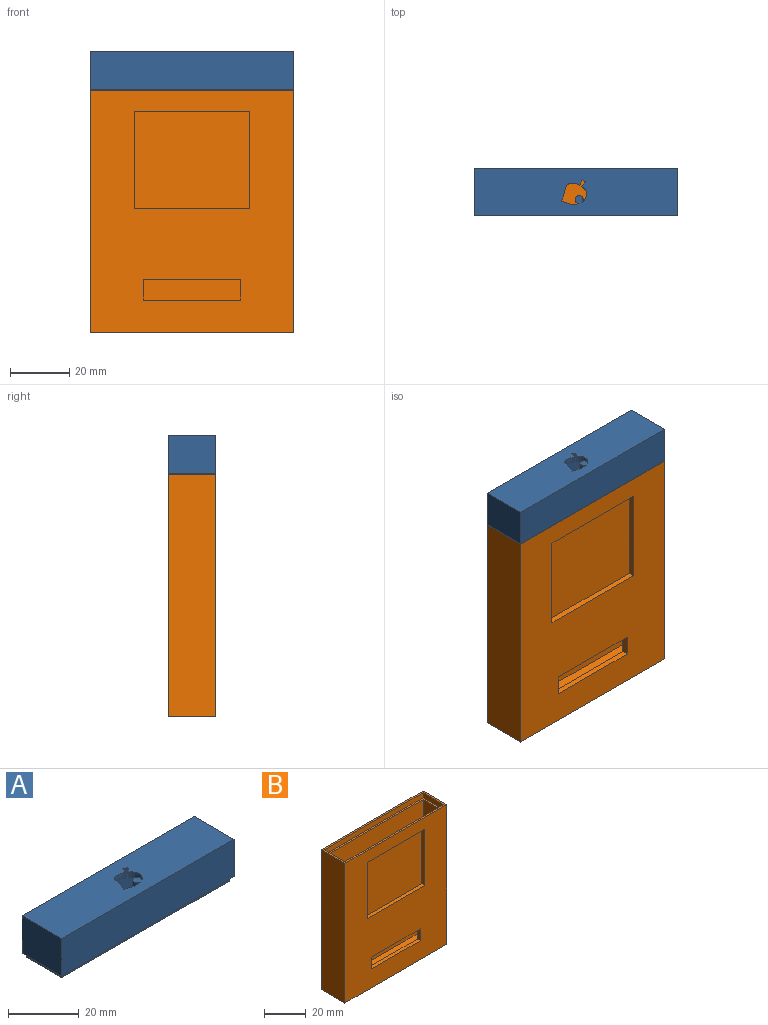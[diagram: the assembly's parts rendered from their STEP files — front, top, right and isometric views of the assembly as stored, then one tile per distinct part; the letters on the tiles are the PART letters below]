
ASSEMBLY  parts=2 mates=1
PART A: 26 faces, bbox 69x16x15.5 mm
  f0: plane 65x12mm, normal (0,0,-1), area 737.8mm2, adj f11,f12,f13,f14,f19,f20,f21,f22
  f1: plane 69x16mm, normal (0,0,-1), area 166mm2, adj f2,f3,f4,f5,f7,f8,f9,f10
  f2: plane 69x13mm, normal (0,1,0), area 897mm2, adj f1,f3,f5,f6
  f3: plane 16x13mm, normal (-1,0,0), area 208mm2, adj f1,f2,f4,f6
  f4: plane 69x13mm, normal (0,-1,0), area 897mm2, adj f1,f3,f5,f6
  f5: plane 16x13mm, normal (1,0,0), area 208mm2, adj f1,f2,f4,f6
  f6: plane 69x16mm, normal (0,0,1), area 1061.8mm2, adj f2,f3,f4,f5,f19,f20,f21,f22
  f7: plane 14x1.5mm, normal (-1,0,0), area 21mm2, adj f1,f8,f10,f15
  f8: plane 67x1.5mm, normal (0,1,0), area 100.5mm2, adj f1,f7,f9,f17
  f9: plane 14x1.5mm, normal (1,0,0), area 21mm2, adj f1,f8,f10,f18
  f10: plane 67x1.5mm, normal (0,-1,0), area 100.5mm2, adj f1,f7,f9,f16
  f11: plane 13.5x12mm, normal (-1,0,0), area 162mm2, adj f0,f12,f14,f18
  f12: plane 65x13.5mm, normal (0,1,0), area 877.5mm2, adj f0,f11,f13,f16
  f13: plane 13.5x12mm, normal (1,0,0), area 162mm2, adj f0,f12,f14,f15
  f14: plane 65x13.5mm, normal (0,-1,0), area 877.5mm2, adj f0,f11,f13,f17
  f15: plane 14x1mm, normal (-0.71,0,-0.71), area 18.4mm2, adj f7,f13,f16,f17
  f16: plane 67x1mm, normal (0,-0.71,-0.71), area 93.3mm2, adj f10,f12,f15,f18
  f17: plane 67x1mm, normal (0,0.71,-0.71), area 93.3mm2, adj f8,f14,f15,f18
  f18: plane 14x1mm, normal (0.71,0,-0.71), area 18.4mm2, adj f9,f11,f16,f17
  f19: extruded ~2.77x2.69mm, area 14.4mm2, adj f0,f6,f20,f25
  f20: extruded ~5.43x2mm, area 13.1mm2, adj f0,f6,f19,f21
  f21: plane 2x1.52mm, normal (-0.72,0.7,0), area 4.3mm2, adj f0,f6,f20,f22
  f22: plane 2x1.31mm, normal (-0.49,-0.87,0), area 3mm2, adj f0,f6,f21,f23
  f23: plane 2x1.96mm, normal (0.93,-0.36,0), area 4.2mm2, adj f0,f6,f22,f24
  f24: extruded ~6.38x6.15mm, area 21.2mm2, adj f0,f6,f23,f25
  f25: extruded ~5.87x2mm, area 12mm2, adj f0,f6,f19,f24
PART B: 24 faces, bbox 69x16x82 mm
  f0: plane 82x69mm, normal (0,-1,0), area 4140mm2, adj f2,f3,f4,f5,f16,f17,f18,f19
  f1: plane 77x65mm, normal (0,1,0), area 3487mm2, adj f11,f12,f14,f15,f16,f17,f18,f19
  f2: plane 69x16mm, normal (0,0,1), area 166mm2, adj f0,f3,f5,f6,f7,f8,f9,f10
  f3: plane 82x16mm, normal (-1,0,0), area 1312mm2, adj f0,f2,f4,f6
  f4: plane 69x16mm, normal (0,0,-1), area 1104mm2, adj f0,f3,f5,f6
  f5: plane 82x16mm, normal (1,0,0), area 1312mm2, adj f0,f2,f4,f6
  f6: plane 82x69mm, normal (0,1,0), area 5658mm2, adj f2,f3,f4,f5
  f7: plane 14x3mm, normal (1,0,0), area 42mm2, adj f2,f8,f10,f11
  f8: plane 67x3mm, normal (0,1,0), area 201mm2, adj f2,f7,f9,f11
  f9: plane 14x3mm, normal (-1,0,0), area 42mm2, adj f2,f8,f10,f11
  f10: plane 67x3mm, normal (0,-1,0), area 201mm2, adj f2,f7,f9,f11
  f11: plane 67x14mm, normal (0,0,1), area 158mm2, adj f1,f7,f8,f9,f10,f13,f14,f15
  f12: plane 65x12mm, normal (0,0,1), area 780mm2, adj f1,f13,f14,f15
  f13: plane 77x65mm, normal (0,-1,0), area 5005mm2, adj f11,f12,f14,f15
  f14: plane 77x12mm, normal (-1,0,0), area 924mm2, adj f1,f11,f12,f13
  f15: plane 77x12mm, normal (1,0,0), area 924mm2, adj f1,f11,f12,f13
  f16: plane 39x2mm, normal (0,0,1), area 78mm2, adj f0,f1,f17,f18
  f17: plane 33x2mm, normal (1,0,0), area 66mm2, adj f0,f1,f16,f19
  f18: plane 33x2mm, normal (-1,0,0), area 66mm2, adj f0,f1,f16,f19
  f19: plane 39x2mm, normal (0,0,-1), area 78mm2, adj f0,f1,f17,f18
  f20: plane 33x2mm, normal (0,0,-1), area 66mm2, adj f0,f1,f21,f23
  f21: plane 7x2mm, normal (1,0,0), area 14mm2, adj f0,f1,f20,f22
  f22: plane 33x2mm, normal (0,0,1), area 66mm2, adj f0,f1,f21,f23
  f23: plane 7x2mm, normal (-1,0,0), area 14mm2, adj f0,f1,f20,f22
PLACE A t=(-65.64,3.84,-66.96)mm
PLACE B t=(-65.64,3.84,-158.19)mm
MATE slider B.f2 <-> A.f1  axis (0,0,1) through (1.36,1.84,-78.19)mm
